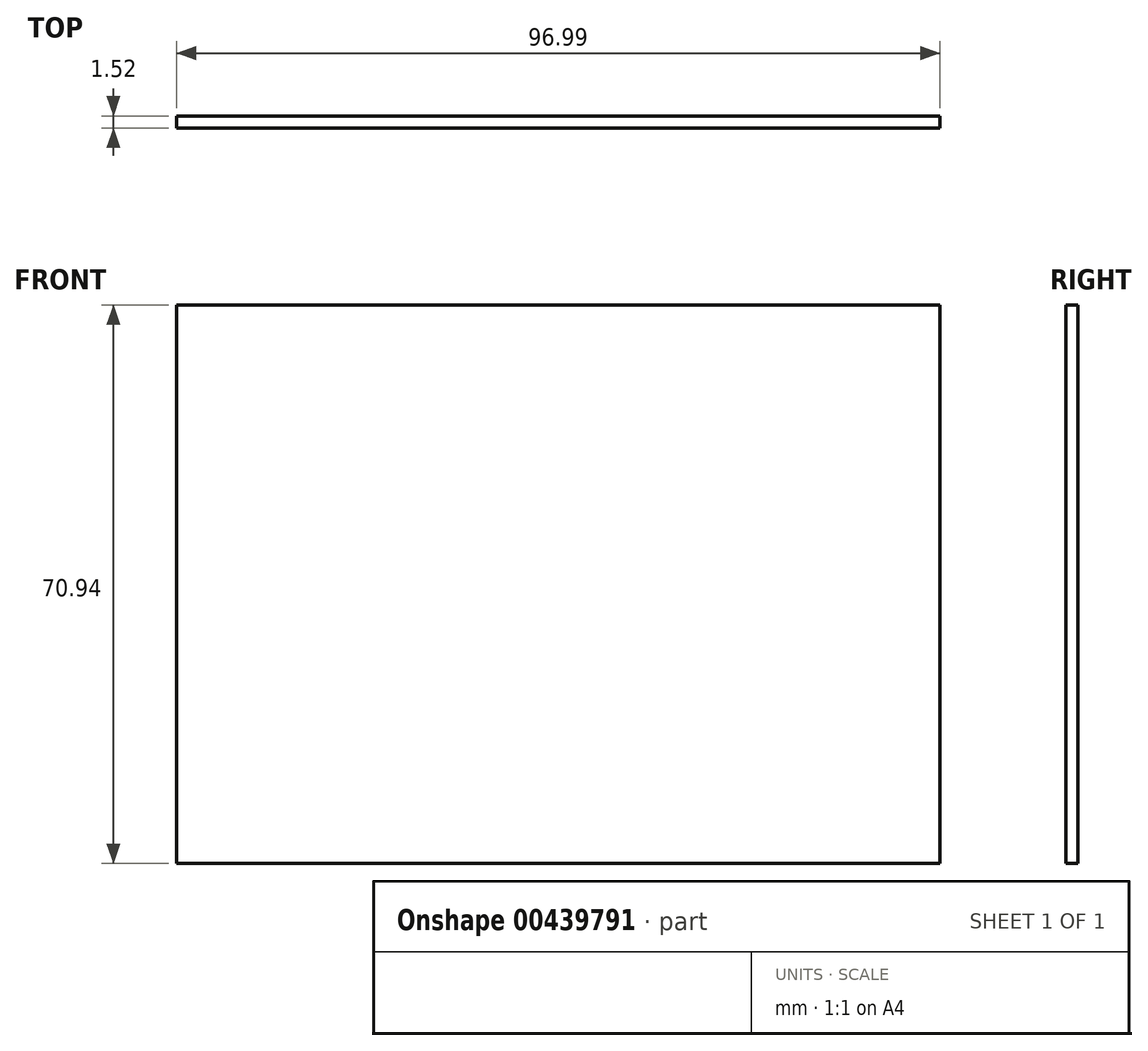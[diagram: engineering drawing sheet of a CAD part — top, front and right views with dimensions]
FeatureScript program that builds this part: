
annotation { "Feature Type Name" : "Feature", "Feature Type Description" : "" }
export const myFeature = defineFeature(function(context is Context, id is Id, definition is map)
    precondition{}
    {
        {
            var Q0;
            Q0=qCreatedBy(makeId("Front.planeOp"),FACE);
            var sketch = newSketch(context, id + "F0", { "sketchPlane" : qUnion([Q0])});
            skLineSegment(sketch, "E0.bottom", {"start": v(-44.2, 31.17) * mm, "end": v(52.8, 31.17) * mm});
            skLineSegment(sketch, "E0.top", {"start": v(-44.2, -39.77) * mm, "end": v(52.8, -39.77) * mm});
            skLineSegment(sketch, "E0.left", {"start": v(-44.2, 31.17) * mm, "end": v(-44.2, -39.77) * mm});
            skLineSegment(sketch, "E0.right", {"start": v(52.8, 31.17) * mm, "end": v(52.8, -39.77) * mm});
            skSolve(sketch);
        }
        {
            var Q0;
            Q0=makeQuery(id+"F0.imprint","IMPRINT",FACE,{"disambiguationData":[TD([[makeQuery(id+"F0.imprint","IMPRINT",EDGE,{"derivedFrom":sQuery(id+"F0.wireOp",EDGE,"E0.bottom")}),-1.0]])]});
            extrude(context, id + "F1", {"entities" : qUnion([Q0]), "depth" : 1.52 * mm});
        }
    });
